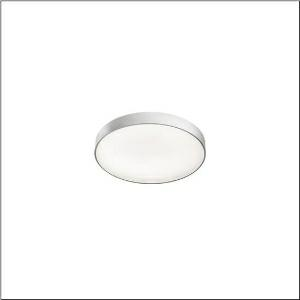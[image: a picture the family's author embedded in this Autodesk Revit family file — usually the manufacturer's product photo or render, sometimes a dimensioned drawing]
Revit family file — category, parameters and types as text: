
# Revit family: round_21_s_51mr34nd0321s
name_source: partatom
category: Lighting Fixtures
units: mm (PartAtom-declared; Revit-internal decimal feet)

## family parameters
Cut with Voids When Loaded = No
Host = Face
Light Source = No
Part Type = Normal
Room Calculation Point = No
Round Connector Dimension = Use Diameter
Shared = No

## types (1)
- Round 21 S (1 x LED, 3660 lm, 28.3 W, 3000K)
    Apparent Load = 28 VA
    CIE Flux Codes = 66 90 98 71 100
    Color Rendering = 80
    Color Temperature = 3000K
    Default Elevation = 1800 mm
    Description = Round 21 S, wall and ceiling luminaire, primary optical cover: micro prismatic cover, of PMMA, transparent, CAT 2 (L<= 3000cd/m²), light emission: direct/indirect distribution, primary light characteristic: symmetric, installation type: suspended mounting, surface-mounted, LED, rated luminous flux: 3.660lm, luminous efficacy: 129lm/W, light colour: 830, colour temperature: 3000K, control gear: DALI 2, with terminal, 5-pole, mains connection: 230V, AC, 50/60Hz, rated input power: 28.3W, housing, of aluminium, coated, silver, diameter: 400mm, height: 62mm, protection rating (complete): IP40, insulation class (complete): insulation class I (protective earthing), certification: CE, impact resistance: IK04, permissible operating ambient temperature: -10..+35°C, packaging unit: 1 piece
    Height = 87 mm
    Lamp = 1 x LED
    Lamp Light Flux = 3660 lm
    Lamp Power = 28.3 W
    Lamp count = 1
    Length = 400 mm
    Luminous efficacy = 129 lm/W
    Manufacturer = Siteco
    ModVariant = No
    Model = 51MR34ND0321S
    Mounting Place = Ceiling
    Mounting Type = Surface mounted
    Number of Poles = 1
    OnlyDefault = Yes
    Power Factor = 1
    Product Name = Round 21 S
    Product group = wall and ceiling luminaire
    ProductGroupID = 304
    Protection Class = Protection class I
    Protection Degree = IP 40
    RLX_Detail_Level = 1
    RLX_Emergency_Light_Flux = 0 lm
    RLX_Emergency_Type = 0
    RLX_Emergency_Type_DB = No
    RlxData = <blob elided: 15113 chars, md5=6ee1b9b7>
    Socket = socket
    Standby Power = 0 W
    System Light Flux = 3660 lm
    System Power = 28 W
    Type Comments = Product without accessories
    Type Image = l_1258336.jpg
    URL = http://relux.com
    VarID = ---
    Voltage = 0 V
    Weight = 0.00 kg
    Width = 0 mm  [stored 0 ft]

note: [stored X ft] marks values corroborated as IEEE doubles in the binary element streams (Revit-internal decimal feet)

## geometry (parser evidence)
native form markers: Sweep x14
no freeform markers — native parametric forms only
